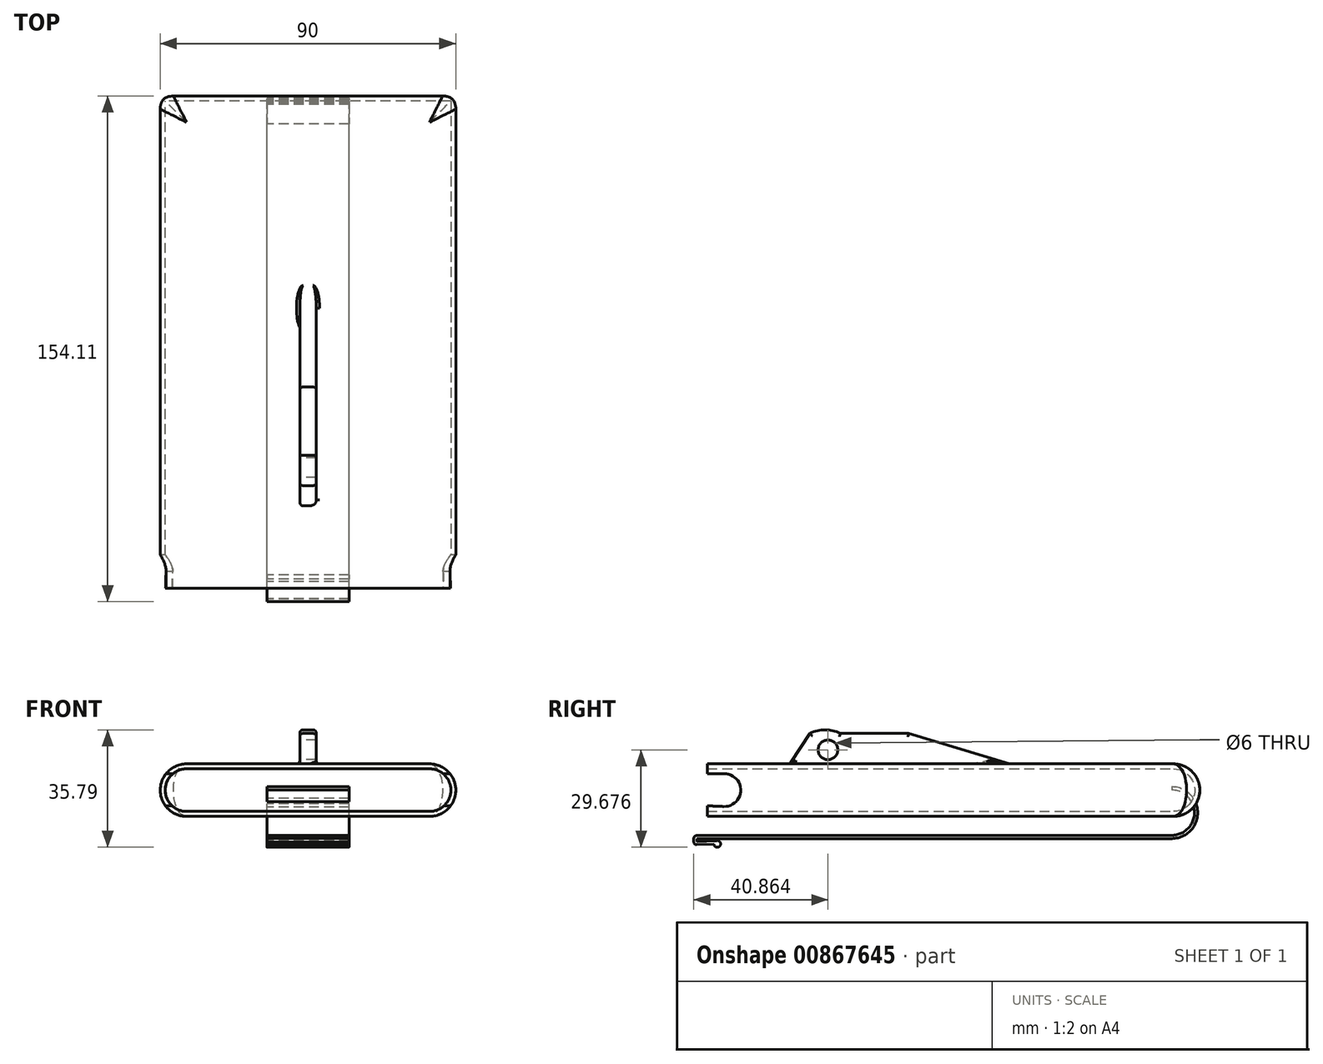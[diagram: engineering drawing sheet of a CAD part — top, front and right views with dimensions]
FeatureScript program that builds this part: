
annotation { "Feature Type Name" : "Feature", "Feature Type Description" : "" }
export const myFeature = defineFeature(function(context is Context, id is Id, definition is map)
    precondition{}
    {
        {
            var Q0;
            Q0=qCreatedBy(makeId("Front.planeOp"),FACE);
            var sketch = newSketch(context, id + "F0", { "sketchPlane" : qUnion([Q0])});
            skLineSegment(sketch, "E0.bottom", {"start": v(45, 8) * mm, "end": v(-45, 8) * mm});
            skLineSegment(sketch, "E0.top", {"start": v(45, -8) * mm, "end": v(-45, -8) * mm});
            skLineSegment(sketch, "E0.left", {"start": v(45, 8) * mm, "end": v(45, -8) * mm});
            skLineSegment(sketch, "E0.right", {"start": v(-45, 8) * mm, "end": v(-45, -8) * mm});
            skPoint(sketch, "E0.middle", {"position": v(0, 0) * mm});
            skSolve(sketch);
        }
        {
            var Q0;
            Q0=makeQuery(id+"F0.imprint","IMPRINT",FACE,{"disambiguationData":[TD([[makeQuery(id+"F0.imprint","IMPRINT",EDGE,{"derivedFrom":sQuery(id+"F0.wireOp",EDGE,"E0.bottom")}),1.0]])]});
            extrude(context, id + "F1", {"entities" : qUnion([Q0]), "endBound" : BoundingType.SYMMETRIC, "depth" : 150 * mm, "offsetDistance" : 25 * mm});
        }
        {
            var Q0;
            Q0=makeQuery(id+"F1.opExtrude","SWEPT_EDGE",EDGE,{"disambiguationData":[OSD([sQuery(id+"F0.wireOp",EDGE,"E0.bottom"),sQuery(id+"F0.wireOp",EDGE,"E0.right")])]});
            var Q1;
            Q1=makeQuery(id+"F1.opExtrude","SWEPT_EDGE",EDGE,{"disambiguationData":[OSD([sQuery(id+"F0.wireOp",EDGE,"E0.top"),sQuery(id+"F0.wireOp",EDGE,"E0.right")])]});
            var Q2;
            Q2=makeQuery(id+"F1.opExtrude","CAP_EDGE",EDGE,{"disambiguationData":[OSD([sQuery(id+"F0.wireOp",EDGE,"E0.top")])],"isStart":true});
            var Q3;
            Q3=makeQuery(id+"F1.opExtrude","CAP_EDGE",EDGE,{"disambiguationData":[OSD([sQuery(id+"F0.wireOp",EDGE,"E0.bottom")])],"isStart":true});
            var Q4;
            Q4=makeQuery(id+"F1.opExtrude","SWEPT_EDGE",EDGE,{"disambiguationData":[OSD([sQuery(id+"F0.wireOp",EDGE,"E0.bottom"),sQuery(id+"F0.wireOp",EDGE,"E0.left")])]});
            var Q5;
            Q5=makeQuery(id+"F1.opExtrude","SWEPT_EDGE",EDGE,{"disambiguationData":[OSD([sQuery(id+"F0.wireOp",EDGE,"E0.top"),sQuery(id+"F0.wireOp",EDGE,"E0.left")])]});
            fillet(context, id + "F2", {"entities" : qUnion([Q0, Q1, Q2, Q3, Q4, Q5]), "radius" : 8 * mm, "tangentPropagation" : true, "allowEdgeOverflow" : false});
        }
        {
            var Q0;
            Q0=makeQuery(id+"F1.opExtrude","CAP_FACE",FACE,{"disambiguationData":[OSD([sQuery(id+"F0.wireOp",EDGE,"E0.bottom"),sQuery(id+"F0.wireOp",EDGE,"E0.top"),sQuery(id+"F0.wireOp",EDGE,"E0.left"),sQuery(id+"F0.wireOp",EDGE,"E0.right")])],"isStart":false});
            shell(context, id + "F3", {"entities" : qUnion([Q0]), "thickness" : 1.5 * mm});
        }
        {
            var Q0;
            Q0=qCreatedBy(makeId("Right.planeOp"),FACE);
            var sketch = newSketch(context, id + "F4", { "sketchPlane" : qUnion([Q0])});
            skLineSegment(sketch, "E1", {"start": v(-145, 7.27) * mm, "end": v(136.4, 7.27) * mm, "construction": true});
            skLineSegment(sketch, "E2", {"start": v(-50.4, 7.27) * mm, "end": v(-43.7, 17.27) * mm});
            skLineSegment(sketch, "E3", {"start": v(-34.5, 17.27) * mm, "end": v(-13.7, 17.27) * mm});
            skLineSegment(sketch, "E4", {"start": v(-13.7, 17.27) * mm, "end": v(19.6, 7.27) * mm});
            skLineSegment(sketch, "E5", {"start": v(19.6, 7.27) * mm, "end": v(-50.4, 7.27) * mm});
            skCircle(sketch, "E6", {"center": v(-38.25, 12.27) * mm, "radius": 3 * mm});
            skPoint(sketch, "E6.centerSnap0", {"position": v(-47.05, 12.27) * mm});
            skArc(sketch, "E7", {"start": v(-34.5, 17.27) * mm, "mid": v(-39.1, 18.38) * mm, "end": v(-43.7, 17.27) * mm});
            skSolve(sketch);
        }
        {
            var Q0;
            Q0=makeQuery(id+"F4.imprint","IMPRINT",FACE,{"disambiguationData":[TD([[makeQuery(id+"F4.imprint","IMPRINT",EDGE,{"derivedFrom":sQuery(id+"F4.wireOp",EDGE,"E2")}),-1.0]])]});
            extrude(context, id + "F5", {"entities" : qUnion([Q0]), "operationType" : NewBodyOperationType.ADD, "endBound" : BoundingType.SYMMETRIC, "depth" : 5 * mm, "offsetDistance" : 25 * mm});
        }
        {
            var Q0;
            Q0=makeQuery(id+"F5.opExtrude","CAP_EDGE",EDGE,{"disambiguationData":[OSD([sQuery(id+"F4.wireOp",EDGE,"E2")])],"isStart":false});
            var Q1;
            Q1=makeQuery(id+"F5.opExtrude","CAP_EDGE",EDGE,{"disambiguationData":[OSD([sQuery(id+"F4.wireOp",EDGE,"E7")])],"isStart":false});
            var Q2;
            Q2=makeQuery(id+"F5.opExtrude","CAP_EDGE",EDGE,{"disambiguationData":[OSD([sQuery(id+"F4.wireOp",EDGE,"E3")])],"isStart":false});
            var Q3;
            Q3=makeQuery(id+"F5.opExtrude","CAP_EDGE",EDGE,{"disambiguationData":[OSD([sQuery(id+"F4.wireOp",EDGE,"E4")])],"isStart":false});
            var Q4;
            Q4=makeQuery(id+"F5.boolean.opBoolean","INTERSECT",EDGE,{"derivedFrom":[makeQuery(id+"F1.opExtrude","SWEPT_FACE",FACE,{"disambiguationData":[OSD([sQuery(id+"F0.wireOp",EDGE,"E0.bottom")])]}),makeQuery(id+"F5.opExtrude","CAP_FACE",FACE,{"disambiguationData":[OSD([sQuery(id+"F4.wireOp",EDGE,"E2"),sQuery(id+"F4.wireOp",EDGE,"E3"),sQuery(id+"F4.wireOp",EDGE,"E4"),sQuery(id+"F4.wireOp",EDGE,"E5"),sQuery(id+"F4.wireOp",EDGE,"E6"),sQuery(id+"F4.wireOp",EDGE,"E7")])],"isStart":false})]});
            var Q5;
            Q5=makeQuery(id+"F5.opExtrude","CAP_EDGE",EDGE,{"disambiguationData":[OSD([sQuery(id+"F4.wireOp",EDGE,"E2")])],"isStart":true});
            var Q6;
            Q6=makeQuery(id+"F5.opExtrude","CAP_EDGE",EDGE,{"disambiguationData":[OSD([sQuery(id+"F4.wireOp",EDGE,"E7")])],"isStart":true});
            var Q7;
            Q7=makeQuery(id+"F5.opExtrude","CAP_EDGE",EDGE,{"disambiguationData":[OSD([sQuery(id+"F4.wireOp",EDGE,"E3")])],"isStart":true});
            var Q8;
            Q8=makeQuery(id+"F5.opExtrude","CAP_EDGE",EDGE,{"disambiguationData":[OSD([sQuery(id+"F4.wireOp",EDGE,"E4")])],"isStart":true});
            var Q9;
            Q9=makeQuery(id+"F5.boolean.opBoolean","INTERSECT",EDGE,{"derivedFrom":[makeQuery(id+"F1.opExtrude","SWEPT_FACE",FACE,{"disambiguationData":[OSD([sQuery(id+"F0.wireOp",EDGE,"E0.bottom")])]}),makeQuery(id+"F5.opExtrude","SWEPT_FACE",FACE,{"disambiguationData":[OSD([sQuery(id+"F4.wireOp",EDGE,"E4")])]})]});
            fillet(context, id + "F6", {"entities" : qUnion([Q0, Q1, Q2, Q3, Q4, Q5, Q6, Q7, Q8, Q9]), "radius" : 1 * mm, "tangentPropagation" : true, "allowEdgeOverflow" : false});
        }
        {
            var Q0;
            Q0=qCreatedBy(makeId("Right.planeOp"),FACE);
            var sketch = newSketch(context, id + "F7", { "sketchPlane" : qUnion([Q0])});
            skLineSegment(sketch, "E8", {"start": v(-72.32, 0) * mm, "end": v(-38.24, 0) * mm, "construction": true});
            skArc(sketch, "E9", {"start": v(-70, -5) * mm, "mid": v(-64.79, -0.07) * mm, "end": v(-69.87, 5) * mm});
            skLineSegment(sketch, "E10", {"start": v(-69.87, 5) * mm, "end": v(-75.3, 5) * mm});
            skLineSegment(sketch, "E11", {"start": v(-70, -5) * mm, "end": v(-75.3, -4.76) * mm});
            skLineSegment(sketch, "E12", {"start": v(-75.3, -4.76) * mm, "end": v(-75.3, 5) * mm});
            skSolve(sketch);
        }
        {
            var Q0;
            Q0=makeQuery(id+"F7.imprint","IMPRINT",FACE,{"disambiguationData":[TD([[makeQuery(id+"F7.imprint","IMPRINT",EDGE,{"derivedFrom":sQuery(id+"F7.wireOp",EDGE,"E9")}),1.0]])]});
            extrude(context, id + "F8", {"entities" : qUnion([Q0]), "operationType" : NewBodyOperationType.REMOVE, "endBound" : BoundingType.SYMMETRIC, "depth" : 100 * mm, "offsetDistance" : 25 * mm});
        }
        {
            var Q0;
            {var subQ0=sQuery(id+"F0.wireOp",EDGE,"E0.bottom");Q0=makeQuery(id+"F2.opFillet","BLEND_EDGE",EDGE,{"blendedFrom":[makeQuery(id+"F1.opExtrude","SWEPT_EDGE",EDGE,{"disambiguationData":[OSD([subQ0,sQuery(id+"F0.wireOp",EDGE,"E0.right")])]}),makeQuery(id+"F1.opExtrude","CAP_EDGE",EDGE,{"disambiguationData":[OSD([subQ0])],"isStart":true})],"blendedInto":[]});}
            var Q1;
            {var subQ0=sQuery(id+"F0.wireOp",EDGE,"E0.bottom");Q1=makeQuery(id+"F2.opFillet","BLEND_EDGE",EDGE,{"blendedFrom":[makeQuery(id+"F1.opExtrude","SWEPT_EDGE",EDGE,{"disambiguationData":[OSD([subQ0,sQuery(id+"F0.wireOp",EDGE,"E0.left")])]}),makeQuery(id+"F1.opExtrude","CAP_EDGE",EDGE,{"disambiguationData":[OSD([subQ0])],"isStart":true})],"blendedInto":[]});}
            fillet(context, id + "F9", {"entities" : qUnion([Q0, Q1]), "radius" : 4 * mm, "tangentPropagation" : true, "rho" : 0.5, "crossSection" : FilletCrossSection.CONIC, "allowEdgeOverflow" : false});
        }
        {
            var Q0;
            Q0=qCreatedBy(makeId("Right.planeOp"),FACE);
            var sketch = newSketch(context, id + "F10", { "sketchPlane" : qUnion([Q0])});
            skLineSegment(sketch, "E13", {"start": v(-77.98, -13.76) * mm, "end": v(66.5, -13.76) * mm});
            skArc(sketch, "E14", {"start": v(66.5, -13.76) * mm, "mid": v(73.38, -6.88) * mm, "end": v(66.5, 0) * mm});
            skArc(sketch, "E15.0", {"start": v(66.5, -14.76) * mm, "mid": v(74.38, -6.88) * mm, "end": v(66.5, 1) * mm});
            skLineSegment(sketch, "E15.1", {"start": v(-78.1, -14.76) * mm, "end": v(66.5, -14.76) * mm});
            skLineSegment(sketch, "E16", {"start": v(66.5, 1) * mm, "end": v(66.5, 0) * mm});
            skLineSegment(sketch, "E17", {"start": v(-78.1, -14.76) * mm, "end": v(-78.1, -15.65) * mm});
            skLineSegment(sketch, "E18", {"start": v(-78.1, -15.65) * mm, "end": v(-72, -15.4) * mm});
            skLineSegment(sketch, "E19.0", {"start": v(-78.31, -16.66) * mm, "end": v(-72.95, -16.44) * mm});
            skLineSegment(sketch, "E20.0", {"start": v(-79.1, -14.67) * mm, "end": v(-79.1, -15.77) * mm});
            skFitSpline(sketch, "E21", {"points": [v(-79.1, -15.77) * mm, v(-78.31, -16.66) * mm], "startDerivative": vector(0.02, -1.3) * mm, "endDerivative": vector(1.63, -0.25) * mm});
            skFitSpline(sketch, "E22", {"points": [v(-77.98, -13.76) * mm, v(-79.1, -14.67) * mm], "startDerivative": vector(-1.95, 0) * mm, "endDerivative": vector(-0.08, -1.37) * mm});
            skArc(sketch, "E23", {"start": v(-72.95, -16.44) * mm, "mid": v(-71.14, -17.03) * mm, "end": v(-72.13, -15.4) * mm});
            skSolve(sketch);
        }
        {
            var Q0;
            Q0=makeQuery(id+"F10.imprint","IMPRINT",FACE,{"disambiguationData":[TD([[makeQuery(id+"F10.imprint","IMPRINT",EDGE,{"derivedFrom":sQuery(id+"F10.wireOp",EDGE,"E13")}),-1.0]])]});
            extrude(context, id + "F11", {"entities" : qUnion([Q0]), "operationType" : NewBodyOperationType.ADD, "endBound" : BoundingType.SYMMETRIC, "depth" : 25 * mm, "offsetDistance" : 25 * mm});
        }
    });
